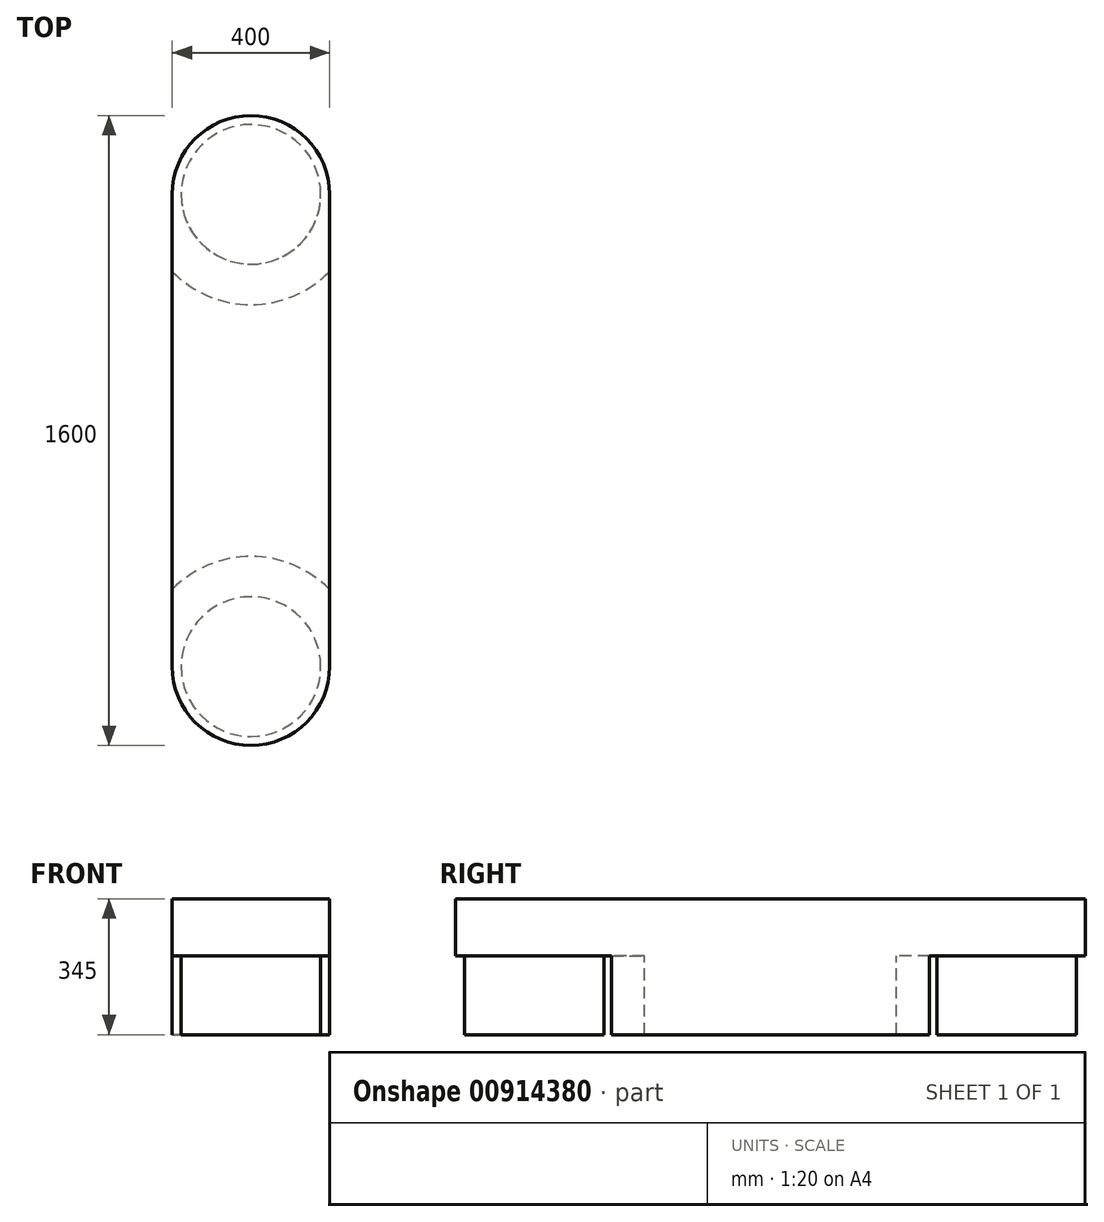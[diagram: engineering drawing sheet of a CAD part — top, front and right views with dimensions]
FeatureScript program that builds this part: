
annotation { "Feature Type Name" : "Feature", "Feature Type Description" : "" }
export const myFeature = defineFeature(function(context is Context, id is Id, definition is map)
    precondition{}
    {
        {
            var Q0;
            Q0=qCreatedBy(makeId("Top.planeOp"),FACE);
            var sketch = newSketch(context, id + "F0", { "sketchPlane" : qUnion([Q0])});
            skLineSegment(sketch, "E0.bottom", {"start": v(-200, 600) * mm, "end": v(200, 600) * mm});
            skLineSegment(sketch, "E0.top", {"start": v(-200, -600) * mm, "end": v(200, -600) * mm});
            skLineSegment(sketch, "E0.left", {"start": v(-200, 600) * mm, "end": v(-200, -600) * mm});
            skLineSegment(sketch, "E0.right", {"start": v(200, 600) * mm, "end": v(200, -600) * mm});
            skPoint(sketch, "E0.middle", {"position": v(0, 0) * mm});
            skArc(sketch, "E1", {"start": v(200, 600) * mm, "mid": v(0, 800) * mm, "end": v(-200, 600) * mm});
            skArc(sketch, "E2", {"start": v(-200, -600) * mm, "mid": v(0, -800) * mm, "end": v(200, -600) * mm});
            skSolve(sketch);
        }
        {
            var Q0;
            Q0 = qSketchRegion(id + "F0", true);
            extrude(context, id + "F1", {"entities" : qUnion([Q0]), "depth" : 145 * mm, "offsetDistance" : 25 * mm});
        }
        {
            var Q0;
            Q0=makeQuery(id+"F1.opExtrude","CAP_FACE",FACE,{"disambiguationData":[OSD([sQuery(id+"F0.wireOp",EDGE,"E0.left"),sQuery(id+"F0.wireOp",EDGE,"E0.right"),sQuery(id+"F0.wireOp",EDGE,"E1"),sQuery(id+"F0.wireOp",EDGE,"E2")])],"isStart":true});
            var sketch = newSketch(context, id + "F2", { "sketchPlane" : qUnion([Q0])});
            skCircle(sketch, "E3", {"center": v(0, 600) * mm, "radius": 177.5 * mm});
            skCircle(sketch, "E4", {"center": v(0, -600) * mm, "radius": 177.5 * mm});
            skArc(sketch, "E5", {"start": v(-200, 404.04) * mm, "mid": v(0.03, 320.08) * mm, "end": v(200, 404.2) * mm});
            skArc(sketch, "E6", {"start": v(200, -404.04) * mm, "mid": v(0, -320) * mm, "end": v(-200, -404.04) * mm});
            skSolve(sketch);
        }
        {
            var Q0;
            Q0 = qSketchRegion(id + "F2", true);
            var Q1;
            {var subQ0=sQuery(id+"F2.wireOp",EDGE,"E5");Q1=makeQuery(id+"F2.imprint","IMPRINT",FACE,{"disambiguationData":[TD([[makeQuery(id+"F2.imprint","IMPRINT",EDGE,{"derivedFrom":subQ0}),-1.0]])]});}
            extrude(context, id + "F3", {"entities" : qUnion([Q0, Q1]), "operationType" : NewBodyOperationType.ADD, "depth" : 200 * mm, "offsetDistance" : 25 * mm});
        }
    });
